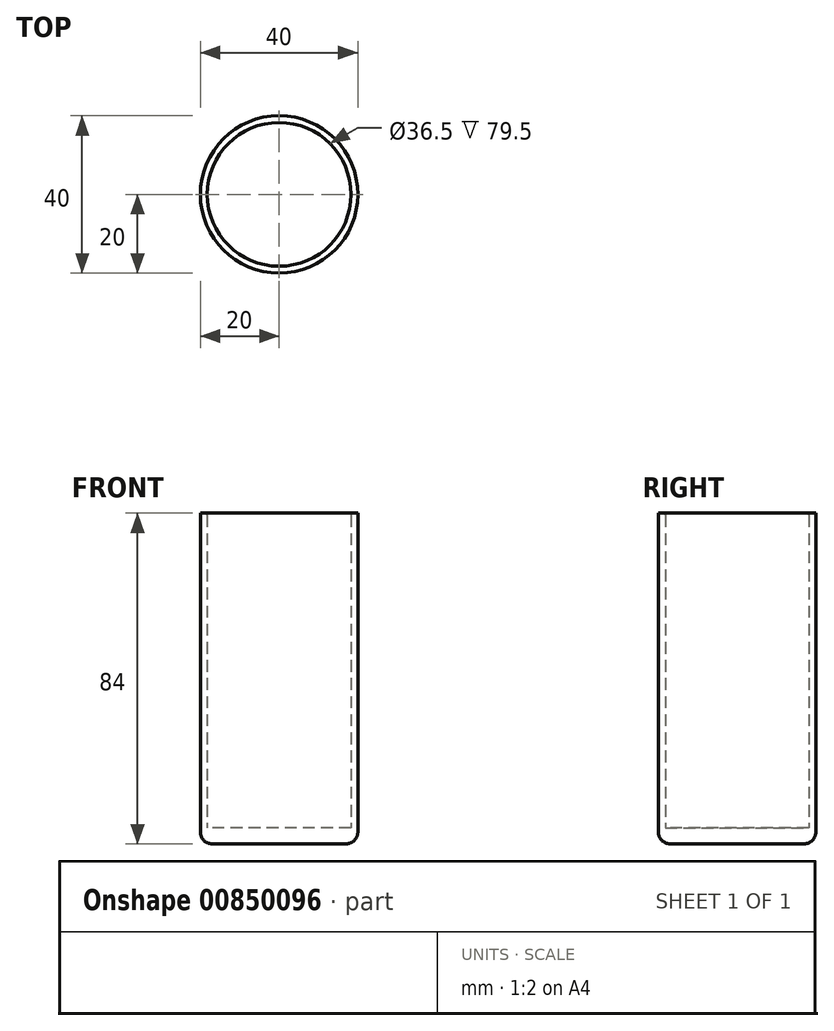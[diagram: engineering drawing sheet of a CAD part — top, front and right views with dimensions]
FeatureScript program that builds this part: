
annotation { "Feature Type Name" : "Feature", "Feature Type Description" : "" }
export const myFeature = defineFeature(function(context is Context, id is Id, definition is map)
    precondition{}
    {
        {
            var Q0;
            Q0=qCreatedBy(makeId("Top.planeOp"),FACE);
            var sketch = newSketch(context, id + "F0", { "sketchPlane" : qUnion([Q0])});
            skCircle(sketch, "E0", {"center": v(0, 0) * mm, "radius": 20 * mm});
            skSolve(sketch);
        }
        {
            var Q0;
            Q0 = qSketchRegion(id + "F0", true);
            extrude(context, id + "F1", {"entities" : qUnion([Q0]), "depth" : 4 * mm, "offsetDistance" : 25 * mm});
        }
        {
            var Q0;
            Q0=makeQuery(id+"F1.opExtrude","CAP_FACE",FACE,{"disambiguationData":[OSD([sQuery(id+"F0.wireOp",EDGE,"E0")])],"isStart":false});
            var sketch = newSketch(context, id + "F2", { "sketchPlane" : qUnion([Q0])});
            skCircle(sketch, "E1", {"center": v(0, 0) * mm, "radius": 18.25 * mm});
            skSolve(sketch);
        }
        {
            var Q0;
            Q0=makeQuery(id+"F2.imprint","IMPRINT",FACE,{"disambiguationData":[TD([[makeQuery(id+"F2.imprint","IMPRINT",EDGE,{"derivedFrom":sQuery(id+"F2.wireOp",EDGE,"E1")}),-1.0]])]});
            extrude(context, id + "F3", {"entities" : qUnion([Q0]), "operationType" : NewBodyOperationType.ADD, "depth" : 80 * mm, "offsetDistance" : 25 * mm});
        }
        {
            var Q0;
            Q0=makeQuery(id+"F3.opExtrude","CAP_EDGE",EDGE,{"disambiguationData":[OSD([sQuery(id+"F2.wireOp",EDGE,"E1")])],"isStart":false});
            fillet(context, id + "F4", {"entities" : qUnion([Q0]), "radius" : .5 * mm, "tangentPropagation" : true, "allowEdgeOverflow" : false});
        }
        {
            var Q0;
            Q0=makeQuery(id+"F1.opExtrude","CAP_EDGE",EDGE,{"disambiguationData":[OSD([sQuery(id+"F0.wireOp",EDGE,"E0")])],"isStart":true});
            fillet(context, id + "F5", {"entities" : qUnion([Q0]), "radius" : 3 * mm, "tangentPropagation" : true, "allowEdgeOverflow" : false});
        }
    });
